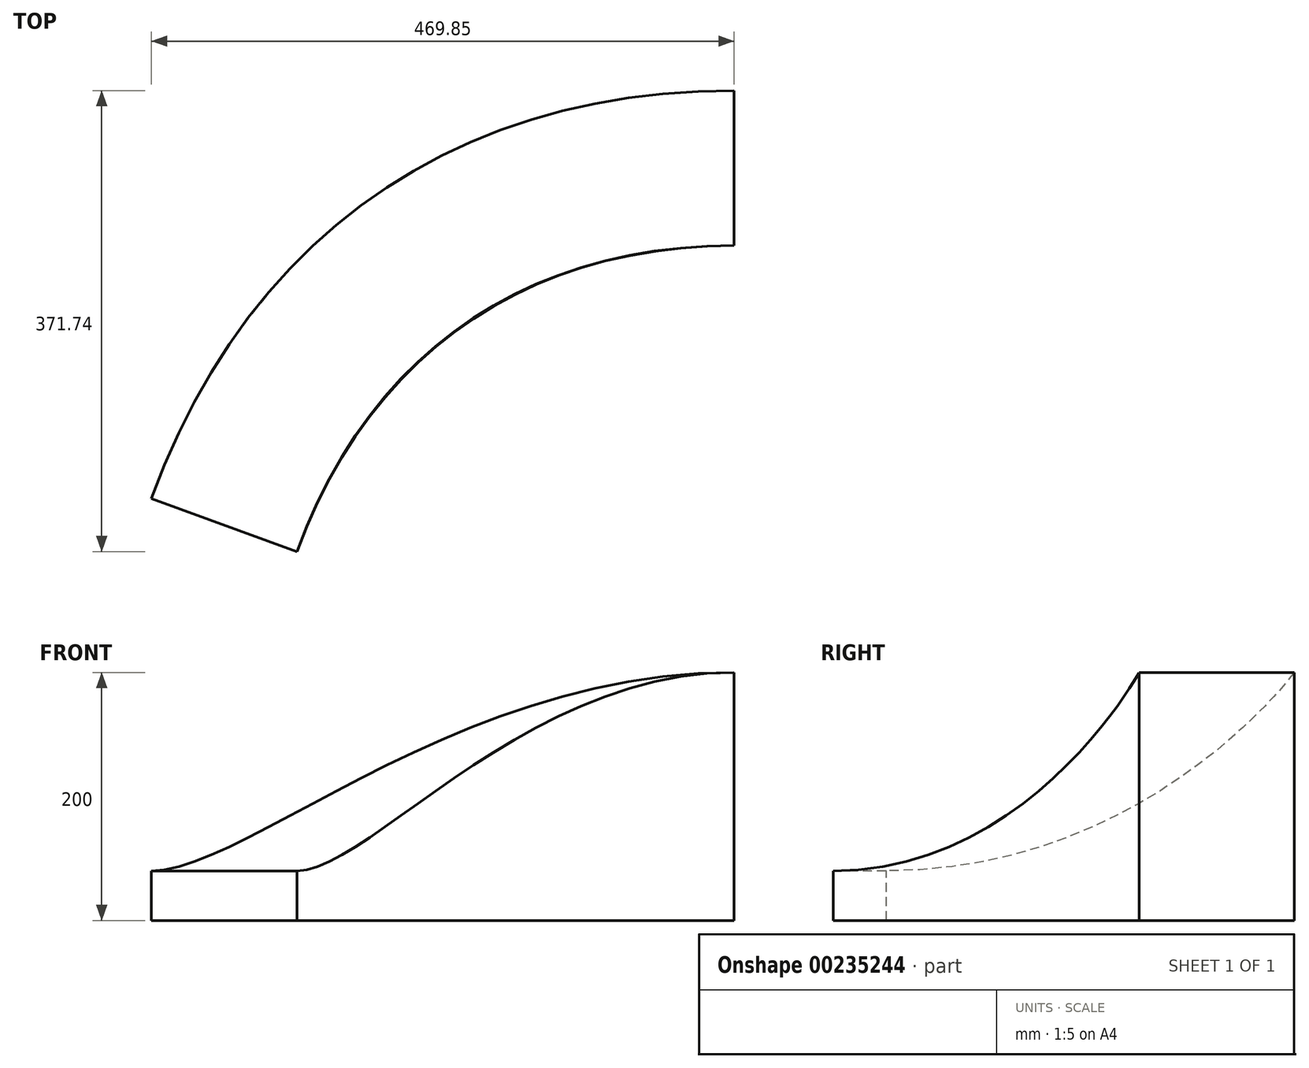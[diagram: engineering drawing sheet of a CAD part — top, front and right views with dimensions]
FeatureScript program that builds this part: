
annotation { "Feature Type Name" : "Feature", "Feature Type Description" : "" }
export const myFeature = defineFeature(function(context is Context, id is Id, definition is map)
    precondition{}
    {
        {
            var Q0;
            Q0=qCreatedBy(makeId("Top.planeOp"),FACE);
            var sketch = newSketch(context, id + "F0", { "sketchPlane" : qUnion([Q0])});
            skCircle(sketch, "E0", {"center": v(0, 0) * mm, "radius": 450 * mm, "construction": true});
            skArc(sketch, "E1", {"start": v(0, 375) * mm, "mid": v(-215.1, 307.18) * mm, "end": v(-352.38, 128.26) * mm});
            skArc(sketch, "E2", {"start": v(0, 500) * mm, "mid": v(-286.79, 409.58) * mm, "end": v(-469.85, 171.01) * mm});
            skLineSegment(sketch, "E3", {"start": v(0, 0) * mm, "end": v(0, 500) * mm, "construction": true});
            skLineSegment(sketch, "E4", {"start": v(0, 0) * mm, "end": v(-469.85, 171.01) * mm, "construction": true});
            skSolve(sketch);
        }
        {
            var Q0;
            Q0=qCreatedBy(makeId("Right.planeOp"),FACE);
            var sketch = newSketch(context, id + "F1", { "sketchPlane" : qUnion([Q0])});
            skLineSegment(sketch, "E5", {"start": v(375, 0) * mm, "end": v(375, 200) * mm});
            skLineSegment(sketch, "E6", {"start": v(375, 200) * mm, "end": v(500, 200) * mm});
            skLineSegment(sketch, "E7", {"start": v(500, 200) * mm, "end": v(500, 0) * mm});
            skLineSegment(sketch, "E8", {"start": v(500, 0) * mm, "end": v(375, 0) * mm});
            skSolve(sketch);
        }
        {
            var Q0;
            Q0=sQuery(id+"F0.wireOp",EDGE,"E4");
            var Q1;
            Q1=qCreatedBy(makeId("Top.planeOp"),FACE);
            cPlane(context, id + "F2", {"entities" : qUnion([Q0, Q1]), "cplaneType" : CPlaneType.LINE_ANGLE, "offset" : 25 * mm, "angle" : 90 * degree, "width" : 150 * mm, "height" : 150 * mm});
        }
        {
            var Q0;
            Q0=qCreatedBy(id+"F2.planeOp",FACE);
            var sketch = newSketch(context, id + "F3", { "sketchPlane" : qUnion([Q0])});
            skLineSegment(sketch, "E9", {"start": v(-500, 0) * mm, "end": v(-500, 40) * mm});
            skLineSegment(sketch, "E10", {"start": v(-500, 40) * mm, "end": v(-375, 40) * mm});
            skLineSegment(sketch, "E11", {"start": v(-375, 40) * mm, "end": v(-375, 0) * mm});
            skLineSegment(sketch, "E12", {"start": v(-375, 0) * mm, "end": v(-500, 0) * mm});
            skSolve(sketch);
        }
        {
            var Q0;
            Q0=makeQuery(id+"F1.imprint","IMPRINT",FACE,{"disambiguationData":[TD([[makeQuery(id+"F1.imprint","IMPRINT",EDGE,{"derivedFrom":sQuery(id+"F1.wireOp",EDGE,"E5")}),-1.0]])]});
            var Q1;
            Q1=makeQuery(id+"F3.imprint","IMPRINT",FACE,{"disambiguationData":[TD([[makeQuery(id+"F3.imprint","IMPRINT",EDGE,{"derivedFrom":sQuery(id+"F3.wireOp",EDGE,"E9")}),-1.0]])]});
            var Q2;
            Q2=sQuery(id+"F0.wireOp",EDGE,"E2");
            var Q3;
            Q3=sQuery(id+"F0.wireOp",EDGE,"E1");
            loft(context, id + "F4", {"startCondition" : LoftEndDerivativeType.NORMAL_TO_PROFILE, "startMagnitude" : 1.4, "endCondition" : LoftEndDerivativeType.NORMAL_TO_PROFILE, "endMagnitude" : 1.4, "sheetProfilesArray" : [{ "sheetProfileEntities" : qUnion([Q0]) }, { "sheetProfileEntities" : qUnion([Q1]) }], "guidesArray" : [{ "guideEntities" : qUnion([Q2]), "guideDerivativeType" : LoftGuideDerivativeType.DEFAULT, "guideDerivativeMagnitude" : 1 }, { "guideEntities" : qUnion([Q3]), "guideDerivativeType" : LoftGuideDerivativeType.DEFAULT, "guideDerivativeMagnitude" : 1 }]});
        }
    });
